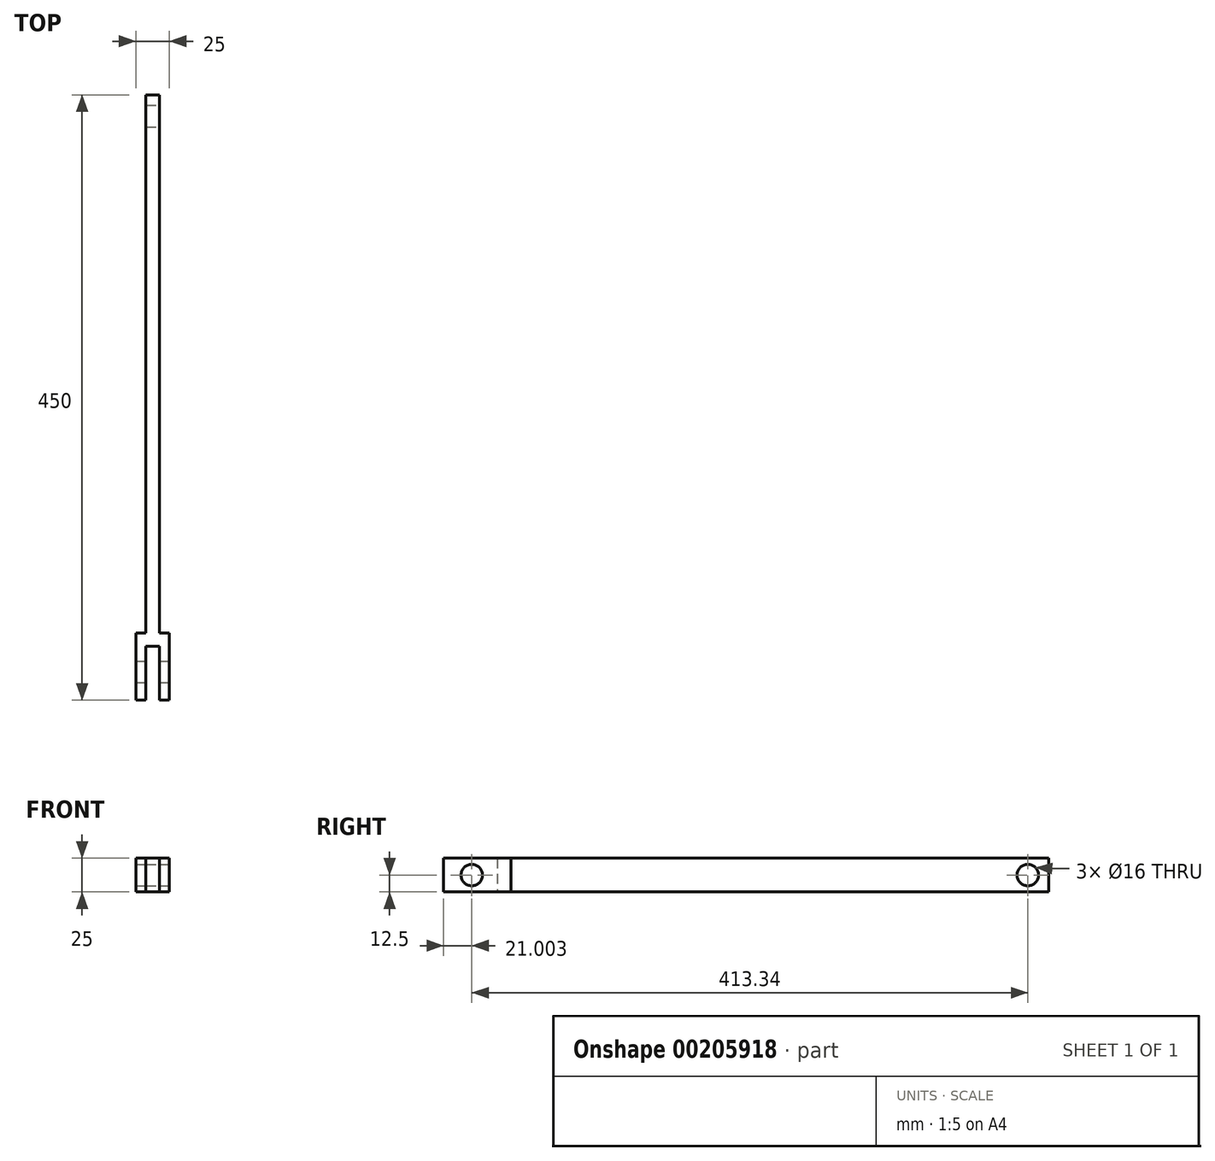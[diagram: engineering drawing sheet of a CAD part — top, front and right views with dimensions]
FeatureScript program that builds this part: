
annotation { "Feature Type Name" : "Feature", "Feature Type Description" : "" }
export const myFeature = defineFeature(function(context is Context, id is Id, definition is map)
    precondition{}
    {
        {
            var Q0;
            Q0=qCreatedBy(makeId("Right.planeOp"),FACE);
            var sketch = newSketch(context, id + "F0", { "sketchPlane" : qUnion([Q0])});
            skLineSegment(sketch, "E0.bottom", {"start": v(200, -12.5) * mm, "end": v(-200, -12.5) * mm});
            skLineSegment(sketch, "E0.top", {"start": v(200, 12.5) * mm, "end": v(-200, 12.5) * mm});
            skLineSegment(sketch, "E0.left", {"start": v(200, -12.5) * mm, "end": v(200, 12.5) * mm});
            skLineSegment(sketch, "E0.right", {"start": v(-200, -12.5) * mm, "end": v(-200, 12.5) * mm});
            skPoint(sketch, "E0.middle", {"position": v(0, 0) * mm});
            skSolve(sketch);
        }
        {
            var Q0;
            Q0=makeQuery(id+"F0.imprint","IMPRINT",FACE,{"disambiguationData":[TD([[makeQuery(id+"F0.imprint","IMPRINT",EDGE,{"derivedFrom":sQuery(id+"F0.wireOp",EDGE,"E0.bottom")}),-1.0]])]});
            extrude(context, id + "F1", {"entities" : qUnion([Q0]), "depth" : 5 * mm, "hasSecondDirection" : true, "secondDirectionOppositeDirection" : true, "secondDirectionDepth" : 5 * mm});
        }
        {
            var Q0;
            Q0=makeQuery(id+"F1.opExtrude","SWEPT_FACE",FACE,{"disambiguationData":[OSD([sQuery(id+"F0.wireOp",EDGE,"E0.right")])]});
            var sketch = newSketch(context, id + "F2", { "sketchPlane" : qUnion([Q0])});
            skLineSegment(sketch, "E1.bottom", {"start": v(12.5, -12.5) * mm, "end": v(-12.5, -12.5) * mm});
            skLineSegment(sketch, "E1.top", {"start": v(12.5, 12.5) * mm, "end": v(-12.5, 12.5) * mm});
            skLineSegment(sketch, "E1.left", {"start": v(12.5, -12.5) * mm, "end": v(12.5, 12.5) * mm});
            skLineSegment(sketch, "E1.right", {"start": v(-12.5, -12.5) * mm, "end": v(-12.5, 12.5) * mm});
            skPoint(sketch, "E1.middle", {"position": v(0, 0) * mm});
            skSolve(sketch);
        }
        {
            var Q0;
            {var subQ2=sQuery(id+"F2.wireOp",EDGE,"E1.right");Q0=makeQuery(id+"F2.imprint","IMPRINT",FACE,{"disambiguationData":[TD([[makeQuery(id+"F2.imprint","IMPRINT",EDGE,{"derivedFrom":subQ2}),-1.0]])]});}
            var Q1;
            {var subQ1=sQuery(id+"F0.wireOp",EDGE,"E0.right");var subQ2=makeQuery(id+"F1.opExtrude","CAP_EDGE",EDGE,{"disambiguationData":[OSD([subQ1])],"isStart":true});Q1=makeQuery(id+"F2.imprint","IMPRINT",FACE,{"disambiguationData":[TD([[makeQuery(id+"F2.imprint","IMPRINT",EDGE,{"derivedFrom":subQ2}),-1.0]])]});}
            var Q2;
            {var subQ2=sQuery(id+"F2.wireOp",EDGE,"E1.left");Q2=makeQuery(id+"F2.imprint","IMPRINT",FACE,{"disambiguationData":[TD([[makeQuery(id+"F2.imprint","IMPRINT",EDGE,{"derivedFrom":subQ2}),1.0]])]});}
            extrude(context, id + "F3", {"entities" : qUnion([Q0, Q1, Q2]), "operationType" : NewBodyOperationType.ADD, "depth" : 10 * mm});
        }
        {
            var Q0;
            Q0=makeQuery(id+"F3.opExtrude","CAP_FACE",FACE,{"disambiguationData":[OSD([sQuery(id+"F2.wireOp",EDGE,"E1.bottom"),sQuery(id+"F2.wireOp",EDGE,"E1.top"),sQuery(id+"F2.wireOp",EDGE,"E1.left"),sQuery(id+"F2.wireOp",EDGE,"E1.right")])],"isStart":false});
            var sketch = newSketch(context, id + "F4", { "sketchPlane" : qUnion([Q0])});
            skLineSegment(sketch, "E2.bottom", {"start": v(-12.5, 12.5) * mm, "end": v(-5, 12.5) * mm});
            skLineSegment(sketch, "E2.top", {"start": v(-12.5, -12.5) * mm, "end": v(-5, -12.5) * mm});
            skLineSegment(sketch, "E2.left", {"start": v(-12.5, 12.5) * mm, "end": v(-12.5, -12.5) * mm});
            skLineSegment(sketch, "E2.right", {"start": v(-5, 12.5) * mm, "end": v(-5, -12.5) * mm});
            skLineSegment(sketch, "E3.bottom", {"start": v(12.5, 12.5) * mm, "end": v(5, 12.5) * mm});
            skLineSegment(sketch, "E3.top", {"start": v(12.5, -12.5) * mm, "end": v(5, -12.5) * mm});
            skLineSegment(sketch, "E3.left", {"start": v(12.5, 12.5) * mm, "end": v(12.5, -12.5) * mm});
            skLineSegment(sketch, "E3.right", {"start": v(5, 12.5) * mm, "end": v(5, -12.5) * mm});
            skSolve(sketch);
        }
        {
            var Q0;
            Q0=makeQuery(id+"F4.imprint","IMPRINT",FACE,{"disambiguationData":[TD([[makeQuery(id+"F4.imprint","IMPRINT",EDGE,{"derivedFrom":sQuery(id+"F4.wireOp",EDGE,"E3.bottom")}),1.0]])]});
            var Q1;
            Q1=makeQuery(id+"F4.imprint","IMPRINT",FACE,{"disambiguationData":[TD([[makeQuery(id+"F4.imprint","IMPRINT",EDGE,{"derivedFrom":sQuery(id+"F4.wireOp",EDGE,"E2.bottom")}),1.0]])]});
            extrude(context, id + "F5", {"entities" : qUnion([Q0, Q1]), "operationType" : NewBodyOperationType.ADD, "depth" : 40 * mm});
        }
        {
            var Q0;
            Q0=makeQuery(id+"F5.boolean.opBoolean","MERGE",FACE,{"derivedFrom":[makeQuery(id+"F3.opExtrude","SWEPT_FACE",FACE,{"disambiguationData":[OSD([sQuery(id+"F2.wireOp",EDGE,"E1.left")])]}),makeQuery(id+"F5.opExtrude","SWEPT_FACE",FACE,{"disambiguationData":[OSD([sQuery(id+"F4.wireOp",EDGE,"E3.left")])]})]});
            var sketch = newSketch(context, id + "F6", { "sketchPlane" : qUnion([Q0])});
            skCircle(sketch, "E4", {"center": v(-229, 0) * mm, "radius": 8 * mm});
            skSolve(sketch);
        }
        {
            var Q0;
            Q0=makeQuery(id+"F6.imprint","IMPRINT",FACE,{"disambiguationData":[TD([[makeQuery(id+"F6.imprint","IMPRINT",EDGE,{"derivedFrom":sQuery(id+"F6.wireOp",EDGE,"E4")}),1.0]])]});
            extrude(context, id + "F7", {"entities" : qUnion([Q0]), "operationType" : NewBodyOperationType.REMOVE, "oppositeDirection" : true, "depth" : 25 * mm});
        }
        {
            var Q0;
            Q0=makeQuery(id+"F1.opExtrude","CAP_FACE",FACE,{"disambiguationData":[OSD([sQuery(id+"F0.wireOp",EDGE,"E0.bottom"),sQuery(id+"F0.wireOp",EDGE,"E0.top"),sQuery(id+"F0.wireOp",EDGE,"E0.left"),sQuery(id+"F0.wireOp",EDGE,"E0.right")])],"isStart":false});
            var sketch = newSketch(context, id + "F8", { "sketchPlane" : qUnion([Q0])});
            skCircle(sketch, "E5", {"center": v(234.89, 0) * mm, "radius": 8 * mm});
            skSolve(sketch);
        }
        {
            var Q0;
            Q0=makeQuery(id+"F8.imprint","IMPRINT",FACE,{"disambiguationData":[TD([[makeQuery(id+"F8.imprint","IMPRINT",EDGE,{"derivedFrom":sQuery(id+"F8.wireOp",EDGE,"E5")}),1.0]])]});
            extrude(context, id + "F9", {"entities" : qUnion([Q0]), "operationType" : NewBodyOperationType.REMOVE, "oppositeDirection" : true, "depth" : 25 * mm});
        }
        {
            var Q0;
            Q0=makeQuery(id+"F1.opExtrude","CAP_FACE",FACE,{"disambiguationData":[OSD([sQuery(id+"F0.wireOp",EDGE,"E0.bottom"),sQuery(id+"F0.wireOp",EDGE,"E0.top"),sQuery(id+"F0.wireOp",EDGE,"E0.left"),sQuery(id+"F0.wireOp",EDGE,"E0.right")])],"isStart":false});
            var sketch = newSketch(context, id + "F10", { "sketchPlane" : qUnion([Q0])});
            skCircle(sketch, "E6", {"center": v(184.34, 0) * mm, "radius": 8 * mm});
            skSolve(sketch);
        }
        {
            var Q0;
            Q0=makeQuery(id+"F10.imprint","IMPRINT",FACE,{"disambiguationData":[TD([[makeQuery(id+"F10.imprint","IMPRINT",EDGE,{"derivedFrom":sQuery(id+"F10.wireOp",EDGE,"E6")}),1.0]])]});
            extrude(context, id + "F11", {"entities" : qUnion([Q0]), "operationType" : NewBodyOperationType.REMOVE, "oppositeDirection" : true, "depth" : 25 * mm});
        }
    });
